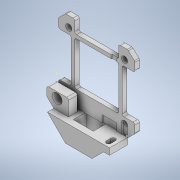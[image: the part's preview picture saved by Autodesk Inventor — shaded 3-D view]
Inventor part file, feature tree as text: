
AUTODESK INVENTOR PART (.ipt)
format: ipt  version: 2020.3 (Build 243373000, 373)  size: 392,704 bytes
history: native  units: mm
features: sketch x16, extrude x14, mirror x2, fillet x1
ambient origin geometry x8: Origin, YZ Plane, XZ Plane, XY Plane, X Axis, Y Axis, Z Axis, Center Point
bodies: Solid1 (feature_tree)
feature tree (33):
  extrude  "Extrusion1"  Depth=2.0mm
  extrude  "Extrusion2"  Depth=2.5mm
  fillet  "Fillet3"  Radius=15.5mm
  mirror  "Mirror3"
  mirror  "Mirror4"
  extrude  "Extrusion3"  Depth=10.0mm TaperAngle=0.0deg
  extrude  "Extrusion4"  Depth=21.2mm
  extrude  "Extrusion5"  Depth=21.2mm
  extrude  "Extrusion6"  Depth=9.0mm
  extrude  "Extrusion10"  Depth=10.0mm
  extrude  "Extrusion11"  Depth=0.5mm TaperAngle=0.0deg
  extrude  "Extrusion12"  Depth=1.0mm TaperAngle=0.0deg
  extrude  "Extrusion13"  Depth=10.0mm
  extrude  "Extrusion15"  Depth=8.0mm
  extrude  "Extrusion16"  Depth=12.0mm
  sketch  "Sketch23"  dims[d54=1.0mm d60=10.0mm]
  sketch  "Sketch24"  dims[d61=6.5mm d62=0.0mm d63=3.5mm d64=0.0mm]
  extrude  "Extrusion18"  Depth=10.0mm
  extrude  "Extrusion19"  Depth=3.5mm TaperAngle=0.0deg
  sketch  "Sketch1"  dims[d0=2.0mm d1=2.0mm]
  sketch  "Sketch2"  dims[d7=2.5mm d8=0.0mm d9=15.5mm d10=15.5mm]
  sketch  "Sketch4"  dims[d11=3.4mm d12=10.0mm d13=0.0mm]
  sketch  "Sketch5"  dims[d19=135.0deg d20=21.2mm]
  sketch  "Sketch6"  dims[d21=21.2mm d22=5.4mm]
  sketch  "Sketch7"  dims[d23=9.0mm d24=9.0mm]
  sketch  "Sketch11"  dims[d25=1.0mm d26=10.0mm]
  sketch  "Sketch12"  dims[d27=3.0mm d28=0.5mm d29=0.0mm]
  sketch  "Sketch13"  dims[d30=5.5mm d32=1.0mm d33=0.0mm]
  sketch  "Sketch16"  dims[d34=3.0mm d35=0.0mm d36=10.0mm]
  sketch  "Sketch18"  dims[d37=4.0mm d38=8.0mm]
  sketch  "Sketch19"  dims[d39=0.5mm d40=0.0mm d53=12.0mm]
  sketch  "Sketch25"  dims[d66=10.0mm d67=0.0mm]
  sketch  "Sketch26"  dims[d68=1.0mm d69=0.0mm d73=5.5mm d74=10.0mm d75=0.0mm d76=1.7mm d77=10.0mm d78=0.0mm d81=45.0deg d83=45.0deg d84=1.5mm d92=14.6mm d93=16.6mm d94=11.2mm d95=3.3mm d96=0.0mm d97=2.5mm d98=3.0mm d99=2.5mm d100=2.5mm d101=10.0mm d102=0.0mm]
